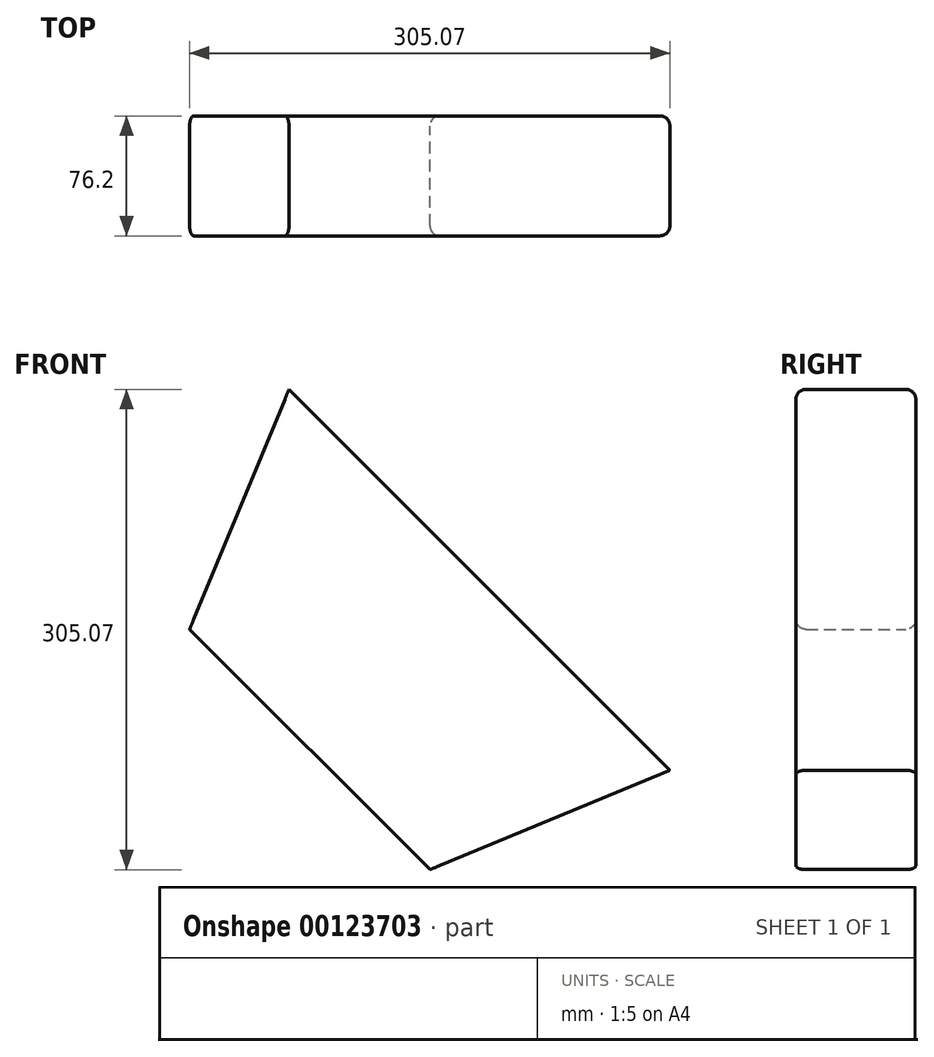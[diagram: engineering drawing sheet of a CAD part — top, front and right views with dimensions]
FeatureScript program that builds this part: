
annotation { "Feature Type Name" : "Feature", "Feature Type Description" : "" }
export const myFeature = defineFeature(function(context is Context, id is Id, definition is map)
    precondition{}
    {
        {
            var Q0;
            Q0=qCreatedBy(makeId("Front.planeOp"),FACE);
            var sketch = newSketch(context, id + "F0", { "sketchPlane" : qUnion([Q0])});
            skLineSegment(sketch, "E0", {"start": v(-75.7, 27.38) * mm, "end": v(-12.58, 179.78) * mm});
            skLineSegment(sketch, "E1", {"start": v(-75.7, 27.38) * mm, "end": v(76.96, -125.29) * mm});
            skLineSegment(sketch, "E2", {"start": v(76.96, -125.29) * mm, "end": v(229.36, -62.16) * mm});
            skLineSegment(sketch, "E3", {"start": v(229.36, -62.16) * mm, "end": v(-12.58, 179.78) * mm});
            skSolve(sketch);
        }
        {
            var Q0;
            Q0=makeQuery(id+"F0.imprint","IMPRINT",FACE,{"disambiguationData":[TD([[makeQuery(id+"F0.imprint","IMPRINT",EDGE,{"derivedFrom":sQuery(id+"F0.wireOp",EDGE,"E0")}),-1.0]])]});
            extrude(context, id + "F1", {"entities" : qUnion([Q0]), "depth" : 76.2 * mm});
        }
        {
            var Q0;
            Q0=makeQuery(id+"F1.opExtrude","CAP_EDGE",EDGE,{"disambiguationData":[OSD([sQuery(id+"F0.wireOp",EDGE,"E3")])],"isStart":false});
            var Q1;
            Q1=makeQuery(id+"F1.opExtrude","CAP_EDGE",EDGE,{"disambiguationData":[OSD([sQuery(id+"F0.wireOp",EDGE,"E1")])],"isStart":false});
            var Q2;
            Q2=makeQuery(id+"F1.opExtrude","CAP_EDGE",EDGE,{"disambiguationData":[OSD([sQuery(id+"F0.wireOp",EDGE,"E3")])],"isStart":true});
            var Q3;
            Q3=makeQuery(id+"F1.opExtrude","CAP_EDGE",EDGE,{"disambiguationData":[OSD([sQuery(id+"F0.wireOp",EDGE,"E1")])],"isStart":true});
            fillet(context, id + "F2", {"entities" : qUnion([Q0, Q1, Q2, Q3]), "radius" : 6.35 * mm, "tangentPropagation" : true, "allowEdgeOverflow" : false});
        }
    });
